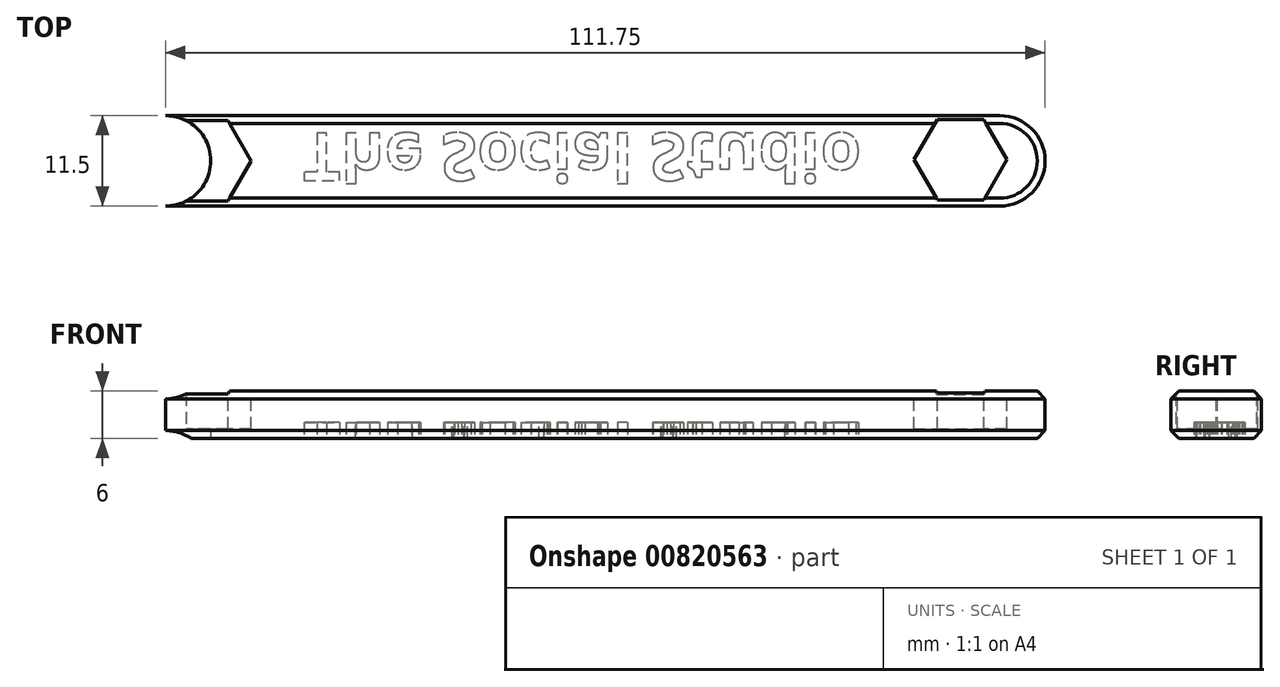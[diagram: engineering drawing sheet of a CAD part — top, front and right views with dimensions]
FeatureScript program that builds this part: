
annotation { "Feature Type Name" : "Feature", "Feature Type Description" : "" }
export const myFeature = defineFeature(function(context is Context, id is Id, definition is map)
    precondition{}
    {
        {
            var Q0;
            Q0=qCreatedBy(makeId("Top.planeOp"),FACE);
            var sketch = newSketch(context, id + "F0", { "sketchPlane" : qUnion([Q0])});
            skLineSegment(sketch, "E0.bottom", {"start": v(-53, 5.75) * mm, "end": v(45, 5.75) * mm});
            skLineSegment(sketch, "E0.top", {"start": v(-53, -5.75) * mm, "end": v(45, -5.75) * mm});
            skPoint(sketch, "E0.middle", {"position": v(0, 0) * mm});
            skPoint(sketch, "E1.visualSharp", {"position": v(-53, 5.75) * mm});
            skPoint(sketch, "E2.visualSharp", {"position": v(53, 5.75) * mm});
            skPoint(sketch, "E3.visualSharp", {"position": v(53, -5.75) * mm});
            skCircle(sketch, "E4", {"center": v(53, 0) * mm, "radius": 5.75 * mm});
            skCircle(sketch, "E5.MirrorC", {"center": v(-53, 0) * mm, "radius": 5.75 * mm});
            skLineSegment(sketch, "E6.MirrorCS", {"start": v(53, 5.75) * mm, "end": v(-45, 5.75) * mm});
            skLineSegment(sketch, "E7.MirrorCS", {"start": v(53, -5.75) * mm, "end": v(-45, -5.75) * mm});
            skSolve(sketch);
        }
        {
            var Q0;
            Q0=makeQuery(id+"F0.imprint","IMPRINT",FACE,{"disambiguationData":[TD([[makeQuery(id+"F0.imprint","IMPRINT",EDGE,{"derivedFrom":sQuery(id+"F0.wireOp",EDGE,"E0.bottom")}),-1.0]])]});
            var Q1;
            {var subQ0=sQuery(id+"F0.wireOp",EDGE,"E5.MirrorC");var subQ1=makeQuery(id+"F0.imprint","INTERSECT",VERTEX,{"derivedFrom":[sQuery(id+"F0.wireOp",EDGE,"E0.bottom"),subQ0]});Q1=makeQuery(id+"F0.imprint","IMPRINT",FACE,{"disambiguationData":[TD([[makeQuery(id+"F0.imprint","IMPRINT",EDGE,{"disambiguationData":[TD([[subQ1,-1.0]])],"derivedFrom":subQ0}),-1.0]])]});}
            var Q2;
            {var subQ0=sQuery(id+"F0.wireOp",EDGE,"E4");var subQ1=makeQuery(id+"F0.imprint","INTERSECT",VERTEX,{"derivedFrom":[subQ0,sQuery(id+"F0.wireOp",EDGE,"E6.MirrorCS")]});Q2=makeQuery(id+"F0.imprint","IMPRINT",FACE,{"disambiguationData":[TD([[makeQuery(id+"F0.imprint","IMPRINT",EDGE,{"disambiguationData":[TD([[subQ1,-1.0]])],"derivedFrom":subQ0}),1.0]])]});}
            extrude(context, id + "F1", {"entities" : qUnion([Q0, Q1, Q2]), "depth" : 6 * mm, "offsetDistance" : 25 * mm});
        }
        {
            var Q0;
            Q0=makeQuery(id+"F1.opExtrude","CAP_FACE",FACE,{"disambiguationData":[OSD([sQuery(id+"F0.wireOp",EDGE,"E0.bottom"),sQuery(id+"F0.wireOp",EDGE,"E0.top"),sQuery(id+"F0.wireOp",EDGE,"E0.left"),sQuery(id+"F0.wireOp",EDGE,"E0.right"),sQuery(id+"F0.wireOp",EDGE,"E1.filletArc"),sQuery(id+"F0.wireOp",EDGE,"E2.filletArc"),sQuery(id+"F0.wireOp",EDGE,"E3.filletArc"),sQuery(id+"F0.wireOp",EDGE,"7a3905ca-0d4d-49d8-8f45-67b2dd19f99b.filletArc")])],"isStart":false});
            var sketch = newSketch(context, id + "F2", { "sketchPlane" : qUnion([Q0])});
            skCircle(sketch, "E8.cCircle", {"center": v(-48, 0) * mm, "radius": 5.9 * mm, "construction": true});
            skLineSegment(sketch, "E8.0", {"start": v(-50.95, 5.1) * mm, "end": v(-45.05, 5.1) * mm});
            skLineSegment(sketch, "E8.1", {"start": v(-45.05, 5.1) * mm, "end": v(-42.1, 0) * mm});
            skLineSegment(sketch, "E8.2", {"start": v(-42.1, 0) * mm, "end": v(-45.05, -5.1) * mm});
            skLineSegment(sketch, "E8.3", {"start": v(-45.05, -5.1) * mm, "end": v(-50.95, -5.1) * mm});
            skLineSegment(sketch, "E8.4", {"start": v(-50.95, -5.1) * mm, "end": v(-53.9, 0) * mm});
            skLineSegment(sketch, "E8.5", {"start": v(-53.9, 0) * mm, "end": v(-50.95, 5.1) * mm});
            skCircle(sketch, "E9.cCircle", {"center": v(48, 0.14) * mm, "radius": 5.9 * mm, "construction": true});
            skLineSegment(sketch, "E9.0", {"start": v(45.05, 5.25) * mm, "end": v(50.95, 5.25) * mm});
            skLineSegment(sketch, "E9.1", {"start": v(50.95, 5.25) * mm, "end": v(53.9, 0.14) * mm});
            skLineSegment(sketch, "E9.2", {"start": v(53.9, 0.14) * mm, "end": v(50.95, -4.97) * mm});
            skLineSegment(sketch, "E9.3", {"start": v(50.95, -4.97) * mm, "end": v(45.05, -4.97) * mm});
            skLineSegment(sketch, "E9.4", {"start": v(45.05, -4.97) * mm, "end": v(42.1, 0.14) * mm});
            skLineSegment(sketch, "E9.5", {"start": v(42.1, 0.14) * mm, "end": v(45.05, 5.25) * mm});
            skSolve(sketch);
        }
        {
            var Q0;
            Q0=qSketchRegion(id+"F2",true);
            extrude(context, id + "F3", {"entities" : qUnion([Q0]), "operationType" : NewBodyOperationType.REMOVE, "oppositeDirection" : true, "depth" : 4.8 * mm, "offsetDistance" : 25 * mm});
        }
        {
            var Q0;
            Q0=makeQuery(id+"F1.opExtrude","CAP_EDGE",EDGE,{"disambiguationData":[OSD([sQuery(id+"F0.wireOp",EDGE,"E0.bottom")])],"isStart":false});
            var Q1;
            Q1=makeQuery(id+"F1.opExtrude","CAP_EDGE",EDGE,{"disambiguationData":[OSD([sQuery(id+"F0.wireOp",EDGE,"E0.bottom")])],"isStart":true});
            chamfer(context, id + "F4", {"entities" : qUnion([Q0, Q1]), "width" : 1 * mm, "tangentPropagation" : true});
        }
        {
            var Q0;
            Q0=makeQuery(id+"F1.opExtrude","CAP_FACE",FACE,{"disambiguationData":[OSD([sQuery(id+"F0.wireOp",EDGE,"E0.bottom"),sQuery(id+"F0.wireOp",EDGE,"E0.top"),sQuery(id+"F0.wireOp",EDGE,"E5.MirrorC"),sQuery(id+"F0.wireOp",EDGE,"E4"),sQuery(id+"F0.wireOp",EDGE,"E6.MirrorCS"),sQuery(id+"F0.wireOp",EDGE,"E7.MirrorCS")])],"isStart":true});
            var sketch = newSketch(context, id + "F5", { "sketchPlane" : qUnion([Q0])});
            skText(sketch, "E10", { "text": "The Social Studio", "fontName": "OpenSans-Bold.ttf"});
            const initialGuessF5  = {"E10": [-0.03556, -0.00352, 1, 0, 0.00605]};
            skSetInitialGuess(sketch, initialGuessF5);
            skSolve(sketch);
        }
        {
            var Q0;
            Q0 = qSketchRegion(id + "F5", true);
            extrude(context, id + "F6", {"entities" : qUnion([Q0]), "operationType" : NewBodyOperationType.REMOVE, "oppositeDirection" : true, "depth" : 2 * mm, "offsetDistance" : 25 * mm});
        }
    });
